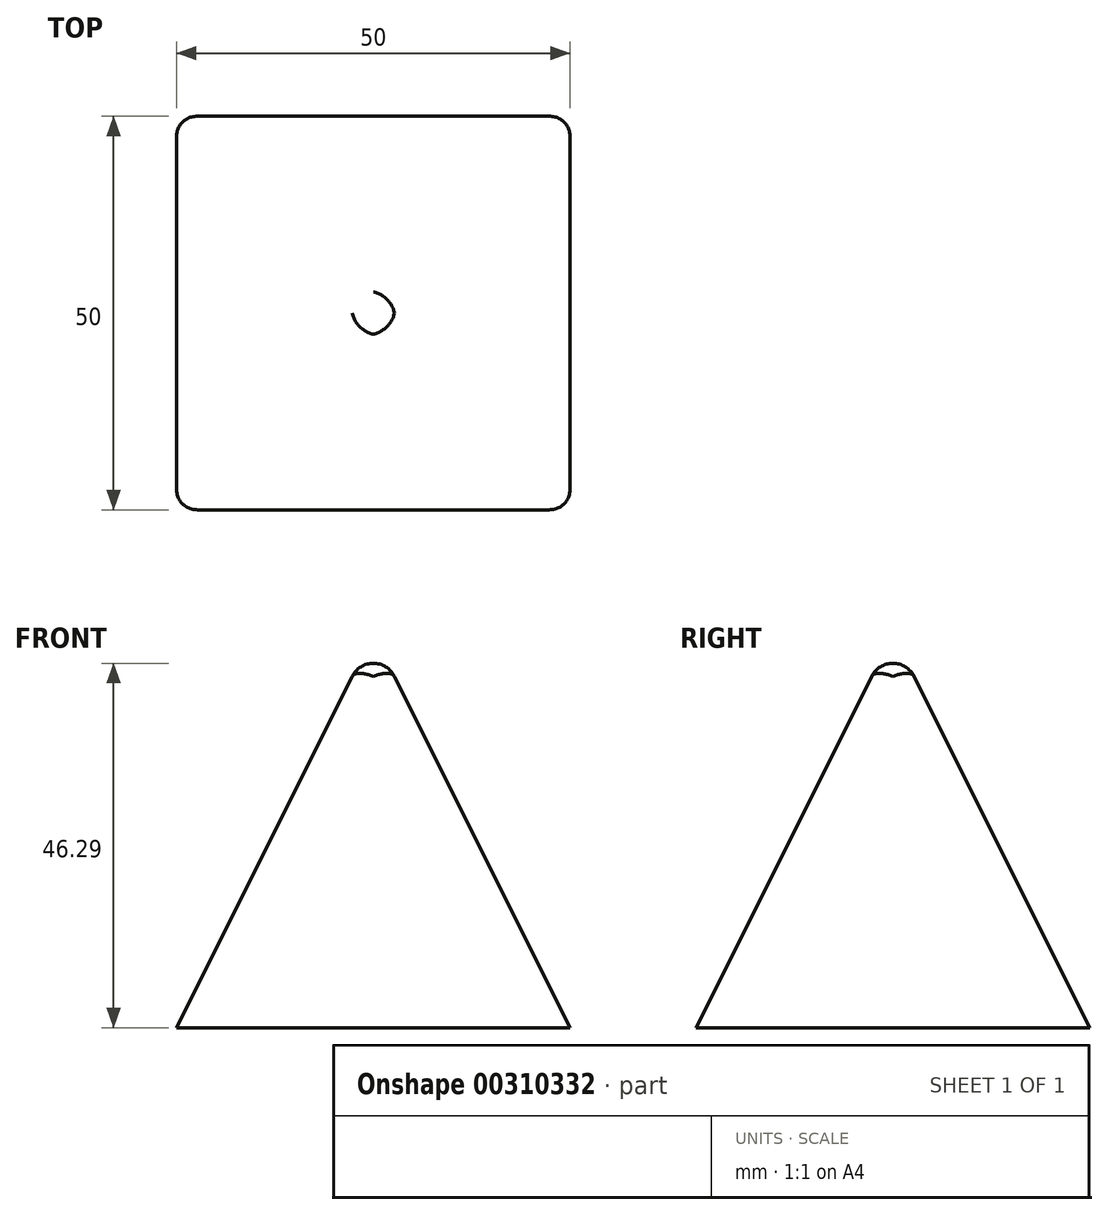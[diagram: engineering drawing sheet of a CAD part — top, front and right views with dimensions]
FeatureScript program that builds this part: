
annotation { "Feature Type Name" : "Feature", "Feature Type Description" : "" }
export const myFeature = defineFeature(function(context is Context, id is Id, definition is map)
    precondition{}
    {
        {
            var Q0;
            Q0=qCreatedBy(makeId("Top.planeOp"),FACE);
            var sketch = newSketch(context, id + "F0", { "sketchPlane" : qUnion([Q0])});
            skLineSegment(sketch, "E0.bottom", {"start": v(-25, 25) * mm, "end": v(25, 25) * mm});
            skLineSegment(sketch, "E0.top", {"start": v(-25, -25) * mm, "end": v(25, -25) * mm});
            skLineSegment(sketch, "E0.left", {"start": v(-25, 25) * mm, "end": v(-25, -25) * mm});
            skLineSegment(sketch, "E0.right", {"start": v(25, 25) * mm, "end": v(25, -25) * mm});
            skSolve(sketch);
        }
        {
            var Q0;
            Q0=qCreatedBy(makeId("Top.planeOp"),FACE);
            cPlane(context, id + "F1", {"entities" : qUnion([Q0]), "cplaneType" : CPlaneType.OFFSET, "offset" : 50 * mm, "width" : 150 * mm, "height" : 150 * mm});
        }
        {
            var Q0;
            Q0=qCreatedBy(id+"F1.planeOp",FACE);
            var sketch = newSketch(context, id + "F2", { "sketchPlane" : qUnion([Q0])});
            skPoint(sketch, "E1", {"position": v(0, 0) * mm});
            skSolve(sketch);
        }
        {
            var Q0;
            Q0=makeQuery(id+"F0.imprint","IMPRINT",FACE,{"disambiguationData":[TD([[makeQuery(id+"F0.imprint","IMPRINT",EDGE,{"derivedFrom":sQuery(id+"F0.wireOp",EDGE,"E0.bottom")}),-1.0]])]});
            var Q1;
            Q1=sQuery(id+"F2.wireOp",VERTEX,"E1");
            loft(context, id + "F3", {"sheetProfilesArray" : [{ "sheetProfileEntities" : qUnion([Q0]) }, { "sheetProfileEntities" : qUnion([Q1]) }]});
        }
        {
            var Q0;
            Q0=makeQuery(id+"F3.opLoft","SWEPT_EDGE",EDGE,{"disambiguationData":[OSD([sQuery(id+"F0.wireOp",EDGE,"E0.bottom"),sQuery(id+"F0.wireOp",EDGE,"E0.left"),sQuery(id+"F2.wireOp",VERTEX,"E1")])]});
            var Q1;
            Q1=makeQuery(id+"F3.opLoft","SWEPT_EDGE",EDGE,{"disambiguationData":[OSD([sQuery(id+"F0.wireOp",EDGE,"E0.top"),sQuery(id+"F0.wireOp",EDGE,"E0.left"),sQuery(id+"F2.wireOp",VERTEX,"E1")])]});
            var Q2;
            Q2=makeQuery(id+"F3.opLoft","SWEPT_EDGE",EDGE,{"disambiguationData":[OSD([sQuery(id+"F0.wireOp",EDGE,"E0.top"),sQuery(id+"F0.wireOp",EDGE,"E0.right"),sQuery(id+"F2.wireOp",VERTEX,"E1")])]});
            var Q3;
            Q3=makeQuery(id+"F3.opLoft","SWEPT_EDGE",EDGE,{"disambiguationData":[OSD([sQuery(id+"F0.wireOp",EDGE,"E0.bottom"),sQuery(id+"F0.wireOp",EDGE,"E0.right"),sQuery(id+"F2.wireOp",VERTEX,"E1")])]});
            fillet(context, id + "F4", {"entities" : qUnion([Q0, Q1, Q2, Q3]), "radius" : 3 * mm, "tangentPropagation" : true, "allowEdgeOverflow" : false});
        }
    });
